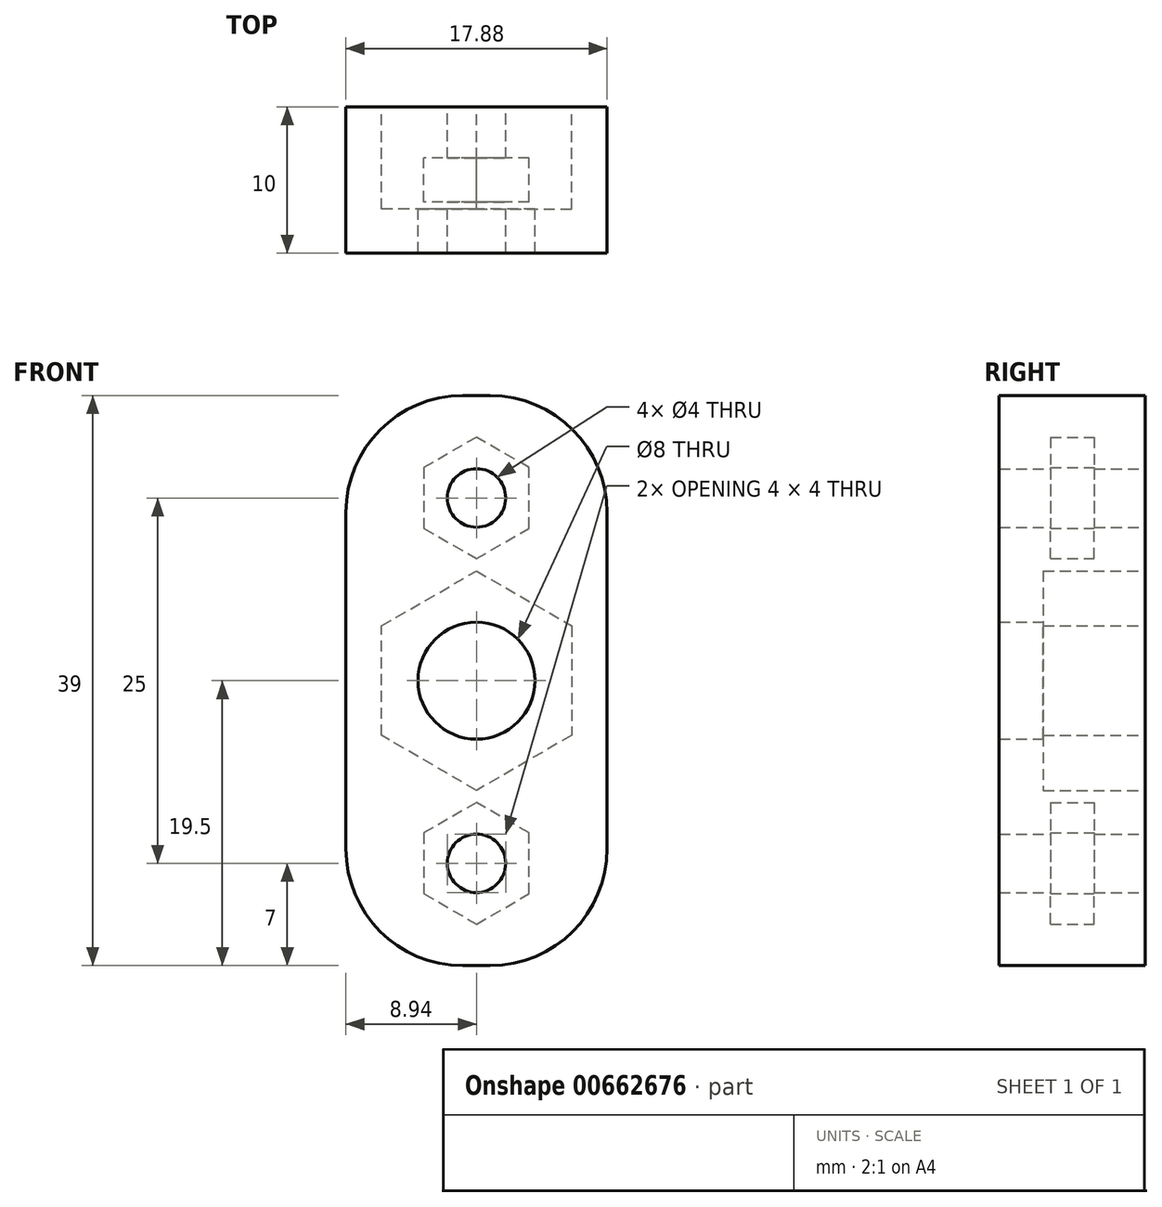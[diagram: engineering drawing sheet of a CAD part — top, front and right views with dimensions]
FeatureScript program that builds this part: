
annotation { "Feature Type Name" : "Feature", "Feature Type Description" : "" }
export const myFeature = defineFeature(function(context is Context, id is Id, definition is map)
    precondition{}
    {
        {
            var Q0;
            Q0=qCreatedBy(makeId("Front.planeOp"),FACE);
            var sketch = newSketch(context, id + "F0", { "sketchPlane" : qUnion([Q0])});
            skCircle(sketch, "E0.cCircle", {"center": v(0, 0) * mm, "radius": 6.5 * mm, "construction": true});
            skLineSegment(sketch, "E0.0", {"start": v(6.5, 3.75) * mm, "end": v(6.5, -3.75) * mm});
            skLineSegment(sketch, "E0.1", {"start": v(6.5, -3.75) * mm, "end": v(0, -7.5) * mm});
            skLineSegment(sketch, "E0.2", {"start": v(0, -7.5) * mm, "end": v(-6.5, -3.75) * mm});
            skLineSegment(sketch, "E0.3", {"start": v(-6.5, -3.75) * mm, "end": v(-6.5, 3.75) * mm});
            skLineSegment(sketch, "E0.4", {"start": v(-6.5, 3.75) * mm, "end": v(0, 7.5) * mm});
            skLineSegment(sketch, "E0.5", {"start": v(0, 7.5) * mm, "end": v(6.5, 3.75) * mm});
            skPoint(sketch, "E0.0.midPoint", {"position": v(6.5, 0) * mm});
            skLineSegment(sketch, "E1.bottom", {"start": v(8.94, -19.5) * mm, "end": v(-8.94, -19.5) * mm});
            skLineSegment(sketch, "E1.top", {"start": v(8.94, 19.5) * mm, "end": v(-8.94, 19.5) * mm});
            skLineSegment(sketch, "E1.left", {"start": v(8.94, -19.5) * mm, "end": v(8.94, 19.5) * mm});
            skLineSegment(sketch, "E1.right", {"start": v(-8.94, -19.5) * mm, "end": v(-8.94, 19.5) * mm});
            skCircle(sketch, "E2", {"center": v(0, 12.5) * mm, "radius": 2 * mm});
            skCircle(sketch, "E3", {"center": v(0, -12.5) * mm, "radius": 2 * mm});
            skSolve(sketch);
        }
        {
            var Q0;
            Q0=qSketchRegion(id+"F0",true);
            extrude(context, id + "F1", {"entities" : qUnion([Q0]), "depth" : 7 * mm});
        }
        {
            var Q0;
            Q0=makeQuery(id+"F1.opExtrude","CAP_FACE",FACE,{"disambiguationData":[OSD([sQuery(id+"F0.wireOp",EDGE,"E0.0"),sQuery(id+"F0.wireOp",EDGE,"E0.1"),sQuery(id+"F0.wireOp",EDGE,"E0.2"),sQuery(id+"F0.wireOp",EDGE,"E0.3"),sQuery(id+"F0.wireOp",EDGE,"E0.4"),sQuery(id+"F0.wireOp",EDGE,"E0.5"),sQuery(id+"F0.wireOp",EDGE,"E1.bottom"),sQuery(id+"F0.wireOp",EDGE,"E1.top"),sQuery(id+"F0.wireOp",EDGE,"E1.left"),sQuery(id+"F0.wireOp",EDGE,"E1.right"),sQuery(id+"F0.wireOp",EDGE,"E2"),sQuery(id+"F0.wireOp",EDGE,"E3")])],"isStart":false});
            var sketch = newSketch(context, id + "F2", { "sketchPlane" : qUnion([Q0])});
            skCircle(sketch, "E4", {"center": v(0, 0) * mm, "radius": 4 * mm});
            skSolve(sketch);
        }
        {
            var Q0;
            Q0=makeQuery(id+"F2.imprint","IMPRINT",FACE,{"disambiguationData":[TD([[makeQuery(id+"F2.imprint","IMPRINT",EDGE,{"derivedFrom":makeQuery(id+"F1.opExtrude","CAP_EDGE",EDGE,{"disambiguationData":[OSD([sQuery(id+"F0.wireOp",EDGE,"E0.0")])],"isStart":false})}),1.0]])]});
            var Q1;
            Q1=makeQuery(id+"F2.imprint","IMPRINT",FACE,{"disambiguationData":[TD([[makeQuery(id+"F2.imprint","IMPRINT",EDGE,{"derivedFrom":sQuery(id+"F2.wireOp",EDGE,"E4")}),-1.0]])]});
            extrude(context, id + "F3", {"entities" : qUnion([Q0, Q1]), "operationType" : NewBodyOperationType.ADD, "depth" : 3 * mm});
        }
        {
            var Q0;
            Q0=makeQuery(id+"F1.opExtrude","CAP_FACE",FACE,{"disambiguationData":[OSD([sQuery(id+"F0.wireOp",EDGE,"E0.0"),sQuery(id+"F0.wireOp",EDGE,"E0.1"),sQuery(id+"F0.wireOp",EDGE,"E0.2"),sQuery(id+"F0.wireOp",EDGE,"E0.3"),sQuery(id+"F0.wireOp",EDGE,"E0.4"),sQuery(id+"F0.wireOp",EDGE,"E0.5"),sQuery(id+"F0.wireOp",EDGE,"E1.bottom"),sQuery(id+"F0.wireOp",EDGE,"E1.top"),sQuery(id+"F0.wireOp",EDGE,"E1.left"),sQuery(id+"F0.wireOp",EDGE,"E1.right"),sQuery(id+"F0.wireOp",EDGE,"E2"),sQuery(id+"F0.wireOp",EDGE,"E3")])],"isStart":true});
            cPlane(context, id + "F4", {"entities" : qUnion([Q0]), "cplaneType" : CPlaneType.OFFSET, "offset" : 5 * mm, "oppositeDirection" : true, "width" : 150 * mm, "height" : 150 * mm});
        }
        {
            var Q0;
            Q0=qCreatedBy(id+"F4.planeOp",FACE);
            var sketch = newSketch(context, id + "F5", { "sketchPlane" : qUnion([Q0])});
            skCircle(sketch, "E5.0", {"center": v(0, -12.5) * mm, "radius": 2 * mm, "construction": true});
            skCircle(sketch, "E6.0", {"center": v(0, 12.5) * mm, "radius": 2 * mm, "construction": true});
            skCircle(sketch, "E7.cCircle", {"center": v(0, -12.5) * mm, "radius": 3.6 * mm, "construction": true});
            skLineSegment(sketch, "E7.0", {"start": v(3.6, -10.42) * mm, "end": v(3.6, -14.58) * mm});
            skLineSegment(sketch, "E7.1", {"start": v(3.6, -14.58) * mm, "end": v(0, -16.66) * mm});
            skLineSegment(sketch, "E7.2", {"start": v(0, -16.66) * mm, "end": v(-3.6, -14.58) * mm});
            skLineSegment(sketch, "E7.3", {"start": v(-3.6, -14.58) * mm, "end": v(-3.6, -10.42) * mm});
            skLineSegment(sketch, "E7.4", {"start": v(-3.6, -10.42) * mm, "end": v(0, -8.34) * mm});
            skLineSegment(sketch, "E7.5", {"start": v(0, -8.34) * mm, "end": v(3.6, -10.42) * mm});
            skPoint(sketch, "E7.0.midPoint", {"position": v(3.6, -12.5) * mm});
            skCircle(sketch, "E8.cCircle", {"center": v(0, 12.5) * mm, "radius": 3.6 * mm, "construction": true});
            skLineSegment(sketch, "E8.0", {"start": v(3.6, 14.58) * mm, "end": v(3.6, 10.42) * mm});
            skLineSegment(sketch, "E8.1", {"start": v(3.6, 10.42) * mm, "end": v(0, 8.34) * mm});
            skLineSegment(sketch, "E8.2", {"start": v(0, 8.34) * mm, "end": v(-3.6, 10.42) * mm});
            skLineSegment(sketch, "E8.3", {"start": v(-3.6, 10.42) * mm, "end": v(-3.6, 14.58) * mm});
            skLineSegment(sketch, "E8.4", {"start": v(-3.6, 14.58) * mm, "end": v(0, 16.66) * mm});
            skLineSegment(sketch, "E8.5", {"start": v(0, 16.66) * mm, "end": v(3.6, 14.58) * mm});
            skPoint(sketch, "E8.0.midPoint", {"position": v(3.6, 12.5) * mm});
            skSolve(sketch);
        }
        {
            var Q0;
            Q0=qSketchRegion(id+"F5",true);
            extrude(context, id + "F6", {"entities" : qUnion([Q0]), "operationType" : NewBodyOperationType.REMOVE, "endBound" : BoundingType.SYMMETRIC, "oppositeDirection" : true, "depth" : 3 * mm});
        }
        {
            var Q0;
            {var subQ0=sQuery(id+"F0.wireOp",EDGE,"E1.right");var subQ1=sQuery(id+"F0.wireOp",EDGE,"E1.bottom");Q0=makeQuery(id+"F3.boolean.opBoolean","MERGE",EDGE,{"derivedFrom":[makeQuery(id+"F1.opExtrude","SWEPT_EDGE",EDGE,{"disambiguationData":[OSD([subQ1,subQ0])]}),makeQuery(id+"F3.opExtrude","SWEPT_EDGE",EDGE,{"disambiguationData":[OSD([subQ1,subQ0])]})]});}
            var Q1;
            {var subQ0=sQuery(id+"F0.wireOp",EDGE,"E1.left");var subQ1=sQuery(id+"F0.wireOp",EDGE,"E1.bottom");Q1=makeQuery(id+"F3.boolean.opBoolean","MERGE",EDGE,{"derivedFrom":[makeQuery(id+"F1.opExtrude","SWEPT_EDGE",EDGE,{"disambiguationData":[OSD([subQ1,subQ0])]}),makeQuery(id+"F3.opExtrude","SWEPT_EDGE",EDGE,{"disambiguationData":[OSD([subQ1,subQ0])]})]});}
            var Q2;
            {var subQ0=sQuery(id+"F0.wireOp",EDGE,"E1.right");var subQ1=sQuery(id+"F0.wireOp",EDGE,"E1.top");Q2=makeQuery(id+"F3.boolean.opBoolean","MERGE",EDGE,{"derivedFrom":[makeQuery(id+"F1.opExtrude","SWEPT_EDGE",EDGE,{"disambiguationData":[OSD([subQ1,subQ0])]}),makeQuery(id+"F3.opExtrude","SWEPT_EDGE",EDGE,{"disambiguationData":[OSD([subQ1,subQ0])]})]});}
            var Q3;
            {var subQ0=sQuery(id+"F0.wireOp",EDGE,"E1.left");var subQ1=sQuery(id+"F0.wireOp",EDGE,"E1.top");Q3=makeQuery(id+"F3.boolean.opBoolean","MERGE",EDGE,{"derivedFrom":[makeQuery(id+"F1.opExtrude","SWEPT_EDGE",EDGE,{"disambiguationData":[OSD([subQ1,subQ0])]}),makeQuery(id+"F3.opExtrude","SWEPT_EDGE",EDGE,{"disambiguationData":[OSD([subQ1,subQ0])]})]});}
            fillet(context, id + "F7", {"entities" : qUnion([Q0, Q1, Q2, Q3]), "radius" : 8 * mm, "tangentPropagation" : true, "allowEdgeOverflow" : false});
        }
    });
